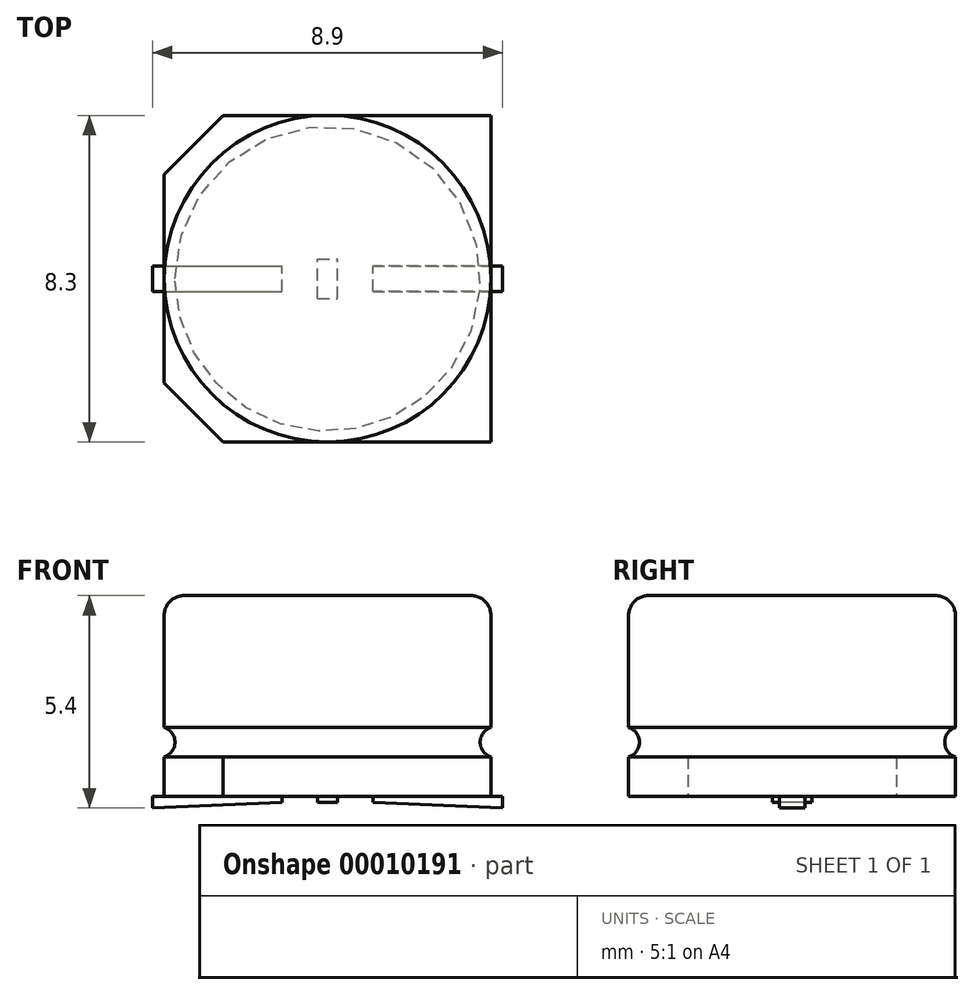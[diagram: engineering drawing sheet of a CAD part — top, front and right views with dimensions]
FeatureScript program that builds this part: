
annotation { "Feature Type Name" : "Feature", "Feature Type Description" : "" }
export const myFeature = defineFeature(function(context is Context, id is Id, definition is map)
    precondition{}
    {
        {
            var Q0;
            Q0=qCreatedBy(makeId("Top.planeOp"),FACE);
            var sketch = newSketch(context, id + "F0", { "sketchPlane" : qUnion([Q0])});
            skLineSegment(sketch, "E0.rect.bottom", {"start": v(-4.15, 4.15) * mm, "end": v(4.15, 4.15) * mm});
            skLineSegment(sketch, "E0.rect.top", {"start": v(-4.15, -4.15) * mm, "end": v(4.15, -4.15) * mm});
            skLineSegment(sketch, "E0.rect.left", {"start": v(-4.15, 4.15) * mm, "end": v(-4.15, -4.15) * mm});
            skLineSegment(sketch, "E0.rect.right", {"start": v(4.15, 4.15) * mm, "end": v(4.15, -4.15) * mm});
            skPoint(sketch, "E0.rect.middle", {"position": v(0, 0) * mm});
            skLineSegment(sketch, "E1", {"start": v(-2.65, 4.15) * mm, "end": v(-4.15, 2.65) * mm});
            skLineSegment(sketch, "E2", {"start": v(-4.15, -2.65) * mm, "end": v(-2.65, -4.15) * mm});
            skSolve(sketch);
        }
        {
            var Q0;
            {var subQ2=sQuery(id+"F0.wireOp",EDGE,"E0.rect.right");Q0=makeQuery(id+"F0.imprint","IMPRINT",FACE,{"disambiguationData":[TD([[makeQuery(id+"F0.imprint","IMPRINT",EDGE,{"derivedFrom":subQ2}),-1.0]])]});}
            extrude(context, id + "F1", {"entities" : qUnion([Q0]), "depth" : 1 * mm});
        }
        {
            var Q0;
            Q0=makeQuery(id+"F1.opExtrude","CAP_FACE",FACE,{"disambiguationData":[OSD([sQuery(id+"F0.wireOp",EDGE,"E0.rect.bottom"),sQuery(id+"F0.wireOp",EDGE,"E0.rect.top"),sQuery(id+"F0.wireOp",EDGE,"E0.rect.left"),sQuery(id+"F0.wireOp",EDGE,"E0.rect.right"),sQuery(id+"F0.wireOp",EDGE,"E1"),sQuery(id+"F0.wireOp",EDGE,"E2")])],"isStart":false});
            var sketch = newSketch(context, id + "F2", { "sketchPlane" : qUnion([Q0])});
            skCircle(sketch, "E3", {"center": v(0, 0) * mm, "radius": 4.15 * mm});
            skSolve(sketch);
        }
        {
            var Q0;
            Q0 = qSketchRegion(id + "F2", true);
            extrude(context, id + "F3", {"entities" : qUnion([Q0]), "operationType" : NewBodyOperationType.ADD, "depth" : 4.1 * mm});
        }
        {
            var Q0;
            Q0=qCreatedBy(makeId("Front.planeOp"),FACE);
            var sketch = newSketch(context, id + "F4", { "sketchPlane" : qUnion([Q0])});
            skArc(sketch, "E4", {"start": v(-4.15, 1) * mm, "mid": v(-3.88, 1.38) * mm, "end": v(-4.15, 1.75) * mm});
            skLineSegment(sketch, "E5", {"start": v(0, 0) * mm, "end": v(-4.15, 0) * mm, "construction": true});
            skLineSegment(sketch, "E6", {"start": v(-4.15, 0) * mm, "end": v(-4.15, 1) * mm, "construction": true});
            skLineSegment(sketch, "E7", {"start": v(-4.15, 1) * mm, "end": v(-4.15, 1.75) * mm});
            skSolve(sketch);
        }
        {
            var Q0;
            Q0 = qSketchRegion(id + "F4", true);
            var Q1;
            Q1=makeQuery(id+"F3.opExtrude","SWEPT_FACE",FACE,{"disambiguationData":[OSD([sQuery(id+"F2.wireOp",EDGE,"E3")])]});
            revolve(context, id + "F5", {"operationType" : NewBodyOperationType.REMOVE, "entities" : qUnion([Q0]), "axis" : qUnion([Q1]), "revolveType" : RevolveType.FULL, "oppositeDirection" : true});
        }
        {
            var Q0;
            Q0=makeQuery(id+"F3.opExtrude","CAP_EDGE",EDGE,{"disambiguationData":[OSD([sQuery(id+"F2.wireOp",EDGE,"E3")])],"isStart":false});
            fillet(context, id + "F6", {"entities" : qUnion([Q0]), "radius" : .5 * mm, "tangentPropagation" : true, "allowEdgeOverflow" : false});
        }
        {
            var Q0;
            Q0=makeQuery(id+"F1.opExtrude","CAP_FACE",FACE,{"disambiguationData":[OSD([sQuery(id+"F0.wireOp",EDGE,"E0.rect.bottom"),sQuery(id+"F0.wireOp",EDGE,"E0.rect.top"),sQuery(id+"F0.wireOp",EDGE,"E0.rect.left"),sQuery(id+"F0.wireOp",EDGE,"E0.rect.right"),sQuery(id+"F0.wireOp",EDGE,"E1"),sQuery(id+"F0.wireOp",EDGE,"E2")])],"isStart":true});
            var sketch = newSketch(context, id + "F7", { "sketchPlane" : qUnion([Q0])});
            skLineSegment(sketch, "E8.bottom", {"start": v(-4.45, 0.33) * mm, "end": v(-1.15, 0.33) * mm});
            skLineSegment(sketch, "E8.top", {"start": v(-4.45, -0.32) * mm, "end": v(-1.15, -0.32) * mm});
            skLineSegment(sketch, "E8.left", {"start": v(-4.45, 0.33) * mm, "end": v(-4.45, -0.32) * mm});
            skLineSegment(sketch, "E8.right", {"start": v(-1.15, 0.32) * mm, "end": v(-1.15, -0.32) * mm});
            skLineSegment(sketch, "E9", {"start": v(0, 0) * mm, "end": v(-1.15, 0) * mm, "construction": true});
            skLineSegment(sketch, "E10", {"start": v(0, 0) * mm, "end": v(0, 4.15) * mm, "construction": true});
            skLineSegment(sketch, "E11.0.MirrorCS", {"start": v(1.15, 0.32) * mm, "end": v(1.15, -0.32) * mm});
            skLineSegment(sketch, "E11.1.MirrorCS", {"start": v(4.45, 0.33) * mm, "end": v(4.45, -0.32) * mm});
            skLineSegment(sketch, "E11.2.MirrorCS", {"start": v(4.45, -0.32) * mm, "end": v(1.15, -0.32) * mm});
            skLineSegment(sketch, "E11.3.MirrorCS", {"start": v(4.45, 0.33) * mm, "end": v(1.15, 0.33) * mm});
            skLineSegment(sketch, "E12.rect.bottom", {"start": v(-0.25, 0.5) * mm, "end": v(0.25, 0.5) * mm});
            skLineSegment(sketch, "E12.rect.top", {"start": v(-0.25, -0.5) * mm, "end": v(0.25, -0.5) * mm});
            skLineSegment(sketch, "E12.rect.left", {"start": v(-0.25, 0.5) * mm, "end": v(-0.25, -0.5) * mm});
            skLineSegment(sketch, "E12.rect.right", {"start": v(0.25, 0.5) * mm, "end": v(0.25, -0.5) * mm});
            skPoint(sketch, "E12.rect.middle", {"position": v(0, 0) * mm});
            skSolve(sketch);
        }
        {
            var Q0;
            Q0 = qSketchRegion(id + "F7", true);
            extrude(context, id + "F8", {"entities" : qUnion([Q0]), "operationType" : NewBodyOperationType.ADD, "depth" : .3 * mm});
        }
        {
            var Q0;
            Q0=makeQuery(id+"F8.opExtrude","SWEPT_FACE",FACE,{"disambiguationData":[OSD([sQuery(id+"F7.wireOp",EDGE,"E11.3.MirrorCS")])]});
            var sketch = newSketch(context, id + "F9", { "sketchPlane" : qUnion([Q0])});
            skLineSegment(sketch, "E13", {"start": v(4.45, -0.3) * mm, "end": v(1.15, -0.15) * mm});
            skLineSegment(sketch, "E14", {"start": v(1.15, -0.15) * mm, "end": v(1.15, -0.3) * mm});
            skLineSegment(sketch, "E15", {"start": v(1.15, -0.3) * mm, "end": v(4.45, -0.3) * mm});
            skLineSegment(sketch, "E16", {"start": v(0, 0) * mm, "end": v(0, -0.76) * mm, "construction": true});
            skLineSegment(sketch, "E17.0.MirrorCS", {"start": v(-1.15, -0.15) * mm, "end": v(-1.15, -0.3) * mm});
            skLineSegment(sketch, "E17.1.MirrorCS", {"start": v(-4.45, -0.3) * mm, "end": v(-1.15, -0.15) * mm});
            skLineSegment(sketch, "E17.2.MirrorCS", {"start": v(-1.15, -0.3) * mm, "end": v(-4.45, -0.3) * mm});
            skLineSegment(sketch, "E18.bottom", {"start": v(-0.25, -0.15) * mm, "end": v(0.25, -0.15) * mm});
            skLineSegment(sketch, "E18.top", {"start": v(-0.25, -0.3) * mm, "end": v(0.25, -0.3) * mm});
            skLineSegment(sketch, "E18.left", {"start": v(-0.25, -0.15) * mm, "end": v(-0.25, -0.3) * mm});
            skLineSegment(sketch, "E18.right", {"start": v(0.25, -0.15) * mm, "end": v(0.25, -0.3) * mm});
            skSolve(sketch);
        }
        {
            var Q0;
            Q0 = qSketchRegion(id + "F9", true);
            extrude(context, id + "F10", {"entities" : qUnion([Q0]), "operationType" : NewBodyOperationType.REMOVE, "endBound" : BoundingType.SYMMETRIC, "oppositeDirection" : true, "depth" : 25 * mm});
        }
    });
